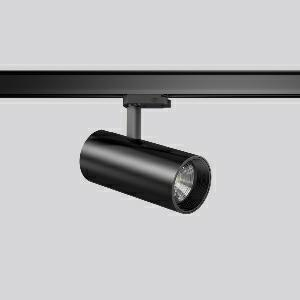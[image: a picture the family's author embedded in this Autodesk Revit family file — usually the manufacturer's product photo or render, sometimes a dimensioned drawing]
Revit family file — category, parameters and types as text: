
# Revit family: deecos_s_mini_742201_003_1_cb6c
name_source: partatom
category: Lighting Fixtures
units: mm (PartAtom-declared; Revit-internal decimal feet)

## family parameters
Cut with Voids When Loaded = No
Host = Face
Light Source = No
Part Type = Normal
Room Calculation Point = No
Round Connector Dimension = Use Diameter
Shared = No

## types (1)
- DEECOS S mini (1 x LED Modul 940, 2450 lm, 4000)
    Apparent Load = 20 VA
    Approval mark = CE
    CIE Flux Codes = 80 99 100 100 100
    Color Rendering = 92
    Color Temperature = 4000
    Default Elevation = 1800 mm
    Description = Series: DEECOS S mini
LED surface-mounted projector in modern design with no visible cooling ribs. Housing: die-cast aluminium, powder-coated. Rotation range: 356°. Swivel range: 90°. Black plastic ring and recessed LED to prevent glare from the side. Optical assembly with lens made of plastic (polycarbonate) for the best homogeneous light distribution - can be changed without tools. Best colour rendering index Ra>90. With multi adaptor for 3-circuit tracks 230 V. Suitable for Track on ceiling, Wall track. High quality converter without flickering and stroboscopic effect. The following accessories can be mounted without use of tools: interchangeable lenses, decorative glasses, honeycomb louvre, clear and frosted diffusers, white interchangeable plastic ring. 
Colour: deep black, matt (RAL 9005)
Diameter: 87 mm
Height: 214 mm
Lamp: LED
Socket: without socket
Colour temperature: 4000K
Colour rendering index (CRI): 92
System power: 20 W
Rated luminous flux: 2450 lm
Luminous efficiency: 123 lm/W
Control gear: Regulated power supply
Protection class: I
Type of protection: IP 20
    Height = 214 mm
    Lamp = 1 x LED Modul 940
    Lamp Light Flux = 2450 lm
    Lamp count = 1
    Length = 87 mm
    Lifetime = 50000 h
    Luminous efficacy = 123 lm/W
    Manufacturer = RZB
    ModVariant = No
    Model = 742201.003.1
    Mounting Place = Ceiling
    Mounting Type = Rail mounted
    Number of Poles = 1
    OnlyDefault = Yes
    Power Factor = 1
    Product Name = DEECOS S mini
    Product group = Track mounted projectors
    ProductGroupID = 301
    Protection Class = Protection class I
    Protection Degree = IP 20
    RLX_Detail_Level = 1
    RLX_Emergency_Light_Flux = 0 lm
    RLX_Emergency_Type = 0
    RLX_Emergency_Type_DB = No
    RlxData = <blob elided: 38657 chars, md5=4f6764b7>
    Socket = socket
    Standby Power = 0 W
    System Light Flux = 2450 lm
    System Power = 20 W
    Type Comments = Product without accessories
    Type Image = 741930.003.jpg
    URL = http://relux.com
    VarID = ---
    Voltage = 230 V
    Voltage Range = 220-240 V
    Weight = 0.00 kg
    Width = 0 mm  [stored 0 ft]

note: [stored X ft] marks values corroborated as IEEE doubles in the binary element streams (Revit-internal decimal feet)

## geometry (parser evidence)
native form markers: Blend x4, Sweep x12
no freeform markers — native parametric forms only
